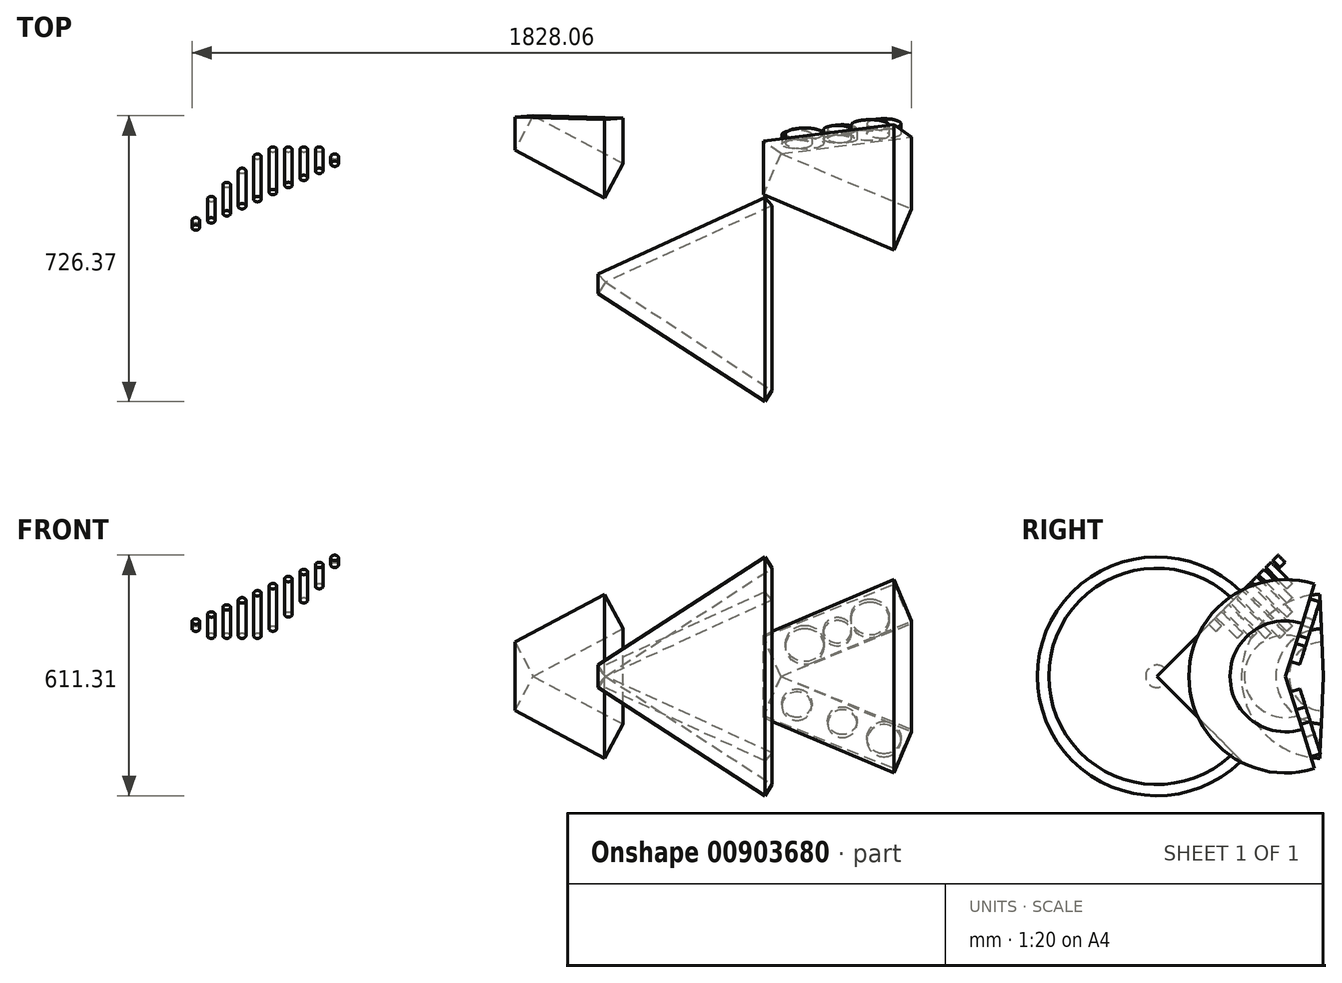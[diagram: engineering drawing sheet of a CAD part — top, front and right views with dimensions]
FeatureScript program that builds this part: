
annotation { "Feature Type Name" : "Feature", "Feature Type Description" : "" }
export const myFeature = defineFeature(function(context is Context, id is Id, definition is map)
    precondition{}
    {
        {
            var Q0;
            Q0=qCreatedBy(makeId("Top.planeOp"),FACE);
            var sketch = newSketch(context, id + "F0", { "sketchPlane" : qUnion([Q0])});
            skLineSegment(sketch, "E0.bottom", {"start": v(100.8, 8.25) * mm, "end": v(328.8, -112.98) * mm});
            skLineSegment(sketch, "E0.top", {"start": v(147.2, 95.54) * mm, "end": v(375.21, -25.7) * mm});
            skLineSegment(sketch, "E0.left", {"start": v(100.8, 8.25) * mm, "end": v(147.2, 95.54) * mm});
            skLineSegment(sketch, "E0.right", {"start": v(328.8, -112.98) * mm, "end": v(375.21, -25.7) * mm});
            skLineSegment(sketch, "E1", {"start": v(147.2, 95.54) * mm, "end": v(426, 95.54) * mm, "construction": true});
            skLineSegment(sketch, "E2", {"start": v(426, 95.54) * mm, "end": v(286.6, 95.54) * mm, "construction": true});
            skLineSegment(sketch, "E3.bottom", {"start": v(776.15, -0.71) * mm, "end": v(1108.48, -141.78) * mm});
            skLineSegment(sketch, "E3.top", {"start": v(731.8, -105.22) * mm, "end": v(1064.12, -246.28) * mm});
            skLineSegment(sketch, "E3.left", {"start": v(776.15, -0.71) * mm, "end": v(731.8, -105.22) * mm});
            skLineSegment(sketch, "E3.right", {"start": v(1108.48, -141.78) * mm, "end": v(1064.12, -246.28) * mm});
            skLineSegment(sketch, "E4.bottom", {"start": v(754.2, -602.2) * mm, "end": v(331.11, -327.43) * mm});
            skLineSegment(sketch, "E4.top", {"start": v(735.61, -630.83) * mm, "end": v(312.51, -356.07) * mm});
            skLineSegment(sketch, "E4.left", {"start": v(754.2, -602.2) * mm, "end": v(735.61, -630.83) * mm});
            skLineSegment(sketch, "E4.right", {"start": v(331.11, -327.43) * mm, "end": v(312.51, -356.07) * mm});
            skLineSegment(sketch, "E5", {"start": v(776.15, -0.71) * mm, "end": v(1137.18, -0.71) * mm, "construction": true});
            skLineSegment(sketch, "E6", {"start": v(331.11, -327.43) * mm, "end": v(835.6, -327.43) * mm, "construction": true});
            skSolve(sketch);
        }
        {
            var Q0;
            Q0=makeQuery(id+"F0.imprint","IMPRINT",FACE,{"disambiguationData":[TD([[makeQuery(id+"F0.imprint","IMPRINT",EDGE,{"derivedFrom":sQuery(id+"F0.wireOp",EDGE,"E0.bottom")}),1.0]])]});
            var Q1;
            Q1=sQuery(id+"F0.wireOp",EDGE,"E1");
            revolve(context, id + "F1", {"surfaceOperationType" : NewSurfaceOperationType.NEW, "entities" : qUnion([Q0]), "axis" : qUnion([Q1]), "revolveType" : RevolveType.SYMMETRIC, "angle" : 175 * degree});
        }
        {
            var Q0;
            Q0=makeQuery(id+"F0.imprint","IMPRINT",FACE,{"disambiguationData":[TD([[makeQuery(id+"F0.imprint","IMPRINT",EDGE,{"derivedFrom":sQuery(id+"F0.wireOp",EDGE,"E3.bottom")}),-1.0]])]});
            var Q1;
            Q1=sQuery(id+"F0.wireOp",EDGE,"E5");
            revolve(context, id + "F2", {"surfaceOperationType" : NewSurfaceOperationType.NEW, "entities" : qUnion([Q0]), "axis" : qUnion([Q1]), "revolveType" : RevolveType.SYMMETRIC, "angle" : 215 * degree});
        }
        {
            var Q0;
            Q0=makeQuery(id+"F0.imprint","IMPRINT",FACE,{"disambiguationData":[TD([[makeQuery(id+"F0.imprint","IMPRINT",EDGE,{"derivedFrom":sQuery(id+"F0.wireOp",EDGE,"E4.bottom")}),1.0]])]});
            var Q1;
            Q1=sQuery(id+"F0.wireOp",EDGE,"E6");
            revolve(context, id + "F3", {"surfaceOperationType" : NewSurfaceOperationType.NEW, "entities" : qUnion([Q0]), "axis" : qUnion([Q1]), "revolveType" : RevolveType.SYMMETRIC, "angle" : 270 * degree});
        }
        {
            var Q0;
            Q0=makeQuery(id+"F2.opRevolve","CAP_FACE",FACE,{"disambiguationData":[OSD([sQuery(id+"F0.wireOp",EDGE,"E3.bottom"),sQuery(id+"F0.wireOp",EDGE,"E3.top"),sQuery(id+"F0.wireOp",EDGE,"E3.left"),sQuery(id+"F0.wireOp",EDGE,"E3.right")])],"isStart":false});
            var sketch = newSketch(context, id + "F4", { "sketchPlane" : qUnion([Q0])});
            skCircle(sketch, "E7", {"center": v(-932.54, -125.78) * mm, "radius": 37.16 * mm});
            skCircle(sketch, "E8", {"center": v(-1038.46, -171.03) * mm, "radius": 43.1 * mm});
            skCircle(sketch, "E9", {"center": v(-817.03, -79.17) * mm, "radius": 37.88 * mm});
            skSolve(sketch);
        }
        {
            var Q0;
            Q0=makeQuery(id+"F4.imprint","IMPRINT",FACE,{"disambiguationData":[TD([[makeQuery(id+"F4.imprint","IMPRINT",EDGE,{"derivedFrom":sQuery(id+"F4.wireOp",EDGE,"E9")}),1.0]])]});
            var Q1;
            Q1=makeQuery(id+"F4.imprint","IMPRINT",FACE,{"disambiguationData":[TD([[makeQuery(id+"F4.imprint","IMPRINT",EDGE,{"derivedFrom":sQuery(id+"F4.wireOp",EDGE,"E7")}),1.0]])]});
            var Q2;
            Q2=makeQuery(id+"F4.imprint","IMPRINT",FACE,{"disambiguationData":[TD([[makeQuery(id+"F4.imprint","IMPRINT",EDGE,{"derivedFrom":sQuery(id+"F4.wireOp",EDGE,"E8")}),1.0]])]});
            extrude(context, id + "F5", {"entities" : qUnion([Q0, Q1, Q2]), "operationType" : NewBodyOperationType.ADD, "depth" : 25.4 * mm, "offsetDistance" : 25.4 * mm});
        }
        {
            var Q0;
            Q0=makeQuery(id+"F2.opRevolve","CAP_FACE",FACE,{"disambiguationData":[OSD([sQuery(id+"F0.wireOp",EDGE,"E3.bottom"),sQuery(id+"F0.wireOp",EDGE,"E3.top"),sQuery(id+"F0.wireOp",EDGE,"E3.left"),sQuery(id+"F0.wireOp",EDGE,"E3.right")])],"isStart":true});
            var sketch = newSketch(context, id + "F6", { "sketchPlane" : qUnion([Q0])});
            skLineSegment(sketch, "E10", {"start": v(-1086.3, 193.1) * mm, "end": v(-753.97, 52.04) * mm, "construction": true});
            skLineSegment(sketch, "E11", {"start": v(-897.95, 174.82) * mm, "end": v(-942.31, 70.32) * mm, "construction": true});
            skLineSegment(sketch, "E12", {"start": v(-814.87, 139.56) * mm, "end": v(-859.23, 35.05) * mm, "construction": true});
            skLineSegment(sketch, "E13", {"start": v(-981.04, 210.09) * mm, "end": v(-1025.4, 105.58) * mm});
            skLineSegment(sketch, "E14.0", {"start": v(-731.8, 104.29) * mm, "end": v(-814.87, 139.56) * mm});
            skLineSegment(sketch, "E15.0", {"start": v(-776.15, -0.21) * mm, "end": v(-1108.48, 140.85) * mm});
            skLineSegment(sketch, "E16.0", {"start": v(-776.15, -0.21) * mm, "end": v(-731.8, 104.29) * mm});
            skLineSegment(sketch, "E17.0", {"start": v(-1108.48, 140.85) * mm, "end": v(-1064.12, 245.35) * mm});
            skLineSegment(sketch, "E18", {"start": v(-897.95, 174.82) * mm, "end": v(-1064.12, 245.35) * mm});
            skLineSegment(sketch, "E19", {"start": v(-814.87, 139.56) * mm, "end": v(-897.95, 174.82) * mm});
            skCircle(sketch, "E20", {"center": v(-1003.22, 157.84) * mm, "radius": 48.44 * mm});
            skCircle(sketch, "E21", {"center": v(-920.13, 122.57) * mm, "radius": 35 * mm});
            skCircle(sketch, "E22", {"center": v(-837.05, 87.3) * mm, "radius": 48.44 * mm});
            skSolve(sketch);
        }
        {
            var Q0;
            Q0=makeQuery(id+"F6.imprint","IMPRINT",FACE,{"disambiguationData":[TD([[makeQuery(id+"F6.imprint","IMPRINT",EDGE,{"derivedFrom":sQuery(id+"F6.wireOp",EDGE,"E22")}),1.0]])]});
            var Q1;
            Q1=makeQuery(id+"F6.imprint","IMPRINT",FACE,{"disambiguationData":[TD([[makeQuery(id+"F6.imprint","IMPRINT",EDGE,{"derivedFrom":sQuery(id+"F6.wireOp",EDGE,"E21")}),1.0]])]});
            var Q2;
            {var subQ0=sQuery(id+"F6.wireOp",EDGE,"E20");var subQ1=sQuery(id+"F6.wireOp",EDGE,"E13");var subQ2=makeQuery(id+"F6.imprint","INTERSECT",VERTEX,{"disambiguationData":[OD(0.0)],"derivedFrom":[subQ1,subQ0]});Q2=makeQuery(id+"F6.imprint","IMPRINT",FACE,{"disambiguationData":[TD([[makeQuery(id+"F6.imprint","IMPRINT",EDGE,{"disambiguationData":[TD([[subQ2,-1.0]])],"derivedFrom":subQ1}),1.0]])]});}
            var Q3;
            {var subQ0=sQuery(id+"F6.wireOp",EDGE,"E20");var subQ1=sQuery(id+"F6.wireOp",EDGE,"E13");var subQ2=makeQuery(id+"F6.imprint","INTERSECT",VERTEX,{"disambiguationData":[OD(0.0)],"derivedFrom":[subQ1,subQ0]});Q3=makeQuery(id+"F6.imprint","IMPRINT",FACE,{"disambiguationData":[TD([[makeQuery(id+"F6.imprint","IMPRINT",EDGE,{"disambiguationData":[TD([[subQ2,-1.0]])],"derivedFrom":subQ1}),-1.0]])]});}
            extrude(context, id + "F7", {"entities" : qUnion([Q0, Q1, Q2, Q3]), "operationType" : NewBodyOperationType.ADD, "depth" : 25.4 * mm, "offsetDistance" : 25.4 * mm});
        }
        {
            var Q0;
            Q0=makeQuery(id+"F3.opRevolve","CAP_FACE",FACE,{"disambiguationData":[OSD([sQuery(id+"F0.wireOp",EDGE,"E4.bottom"),sQuery(id+"F0.wireOp",EDGE,"E4.top"),sQuery(id+"F0.wireOp",EDGE,"E4.left"),sQuery(id+"F0.wireOp",EDGE,"E4.right")])],"isStart":true});
            var sketch = newSketch(context, id + "F8", { "sketchPlane" : qUnion([Q0])});
            skLineSegment(sketch, "E23.0", {"start": v(735.61, -71.87) * mm, "end": v(312.51, 202.9) * mm});
            skLineSegment(sketch, "E24.0", {"start": v(754.2, -43.23) * mm, "end": v(331.11, 231.53) * mm});
            skLineSegment(sketch, "E25.0", {"start": v(331.11, 231.53) * mm, "end": v(312.51, 202.9) * mm});
            skLineSegment(sketch, "E26.0", {"start": v(754.2, -43.23) * mm, "end": v(735.61, -71.87) * mm});
            skCircle(sketch, "E27", {"center": v(709.88, -34.8) * mm, "radius": 9.7 * mm});
            skCircle(sketch, "E28.1.0.0", {"center": v(670.7, -9.36) * mm, "radius": 9.7 * mm});
            skCircle(sketch, "E28.2.0.0", {"center": v(631.51, 16.1) * mm, "radius": 9.7 * mm});
            skCircle(sketch, "E28.3.0.0", {"center": v(592.33, 41.54) * mm, "radius": 9.7 * mm});
            skCircle(sketch, "E28.4.0.0", {"center": v(553.14, 66.98) * mm, "radius": 9.7 * mm});
            skCircle(sketch, "E28.5.0.0", {"center": v(513.96, 92.43) * mm, "radius": 9.7 * mm});
            skCircle(sketch, "E28.6.0.0", {"center": v(474.77, 117.88) * mm, "radius": 9.7 * mm});
            skCircle(sketch, "E28.7.0.0", {"center": v(435.6, 143.32) * mm, "radius": 9.7 * mm});
            skCircle(sketch, "E28.8.0.0", {"center": v(396.4, 168.77) * mm, "radius": 9.7 * mm});
            skCircle(sketch, "E28.9.0.0", {"center": v(357.22, 194.22) * mm, "radius": 9.7 * mm});
            skLineSegment(sketch, "E28.direction1", {"start": v(709.88, -34.8) * mm, "end": v(670.7, -9.36) * mm, "construction": true});
            skLineSegment(sketch, "E29", {"start": v(321.81, 217.21) * mm, "end": v(744.91, -57.55) * mm, "construction": true});
            skSolve(sketch);
        }
        {
            var Q0;
            Q0=makeQuery(id+"F8.imprint","IMPRINT",FACE,{"disambiguationData":[TD([[makeQuery(id+"F8.imprint","IMPRINT",EDGE,{"derivedFrom":sQuery(id+"F8.wireOp",EDGE,"E27")}),1.0]])]});
            var Q1;
            Q1=makeQuery(id+"F8.imprint","IMPRINT",FACE,{"disambiguationData":[TD([[makeQuery(id+"F8.imprint","IMPRINT",EDGE,{"derivedFrom":sQuery(id+"F8.wireOp",EDGE,"E28.1.0.0")}),1.0]])]});
            var Q2;
            Q2=makeQuery(id+"F8.imprint","IMPRINT",FACE,{"disambiguationData":[TD([[makeQuery(id+"F8.imprint","IMPRINT",EDGE,{"derivedFrom":sQuery(id+"F8.wireOp",EDGE,"E28.2.0.0")}),1.0]])]});
            var Q3;
            Q3=makeQuery(id+"F8.imprint","IMPRINT",FACE,{"disambiguationData":[TD([[makeQuery(id+"F8.imprint","IMPRINT",EDGE,{"derivedFrom":sQuery(id+"F8.wireOp",EDGE,"E28.3.0.0")}),1.0]])]});
            var Q4;
            Q4=makeQuery(id+"F8.imprint","IMPRINT",FACE,{"disambiguationData":[TD([[makeQuery(id+"F8.imprint","IMPRINT",EDGE,{"derivedFrom":sQuery(id+"F8.wireOp",EDGE,"E28.4.0.0")}),1.0]])]});
            var Q5;
            Q5=makeQuery(id+"F8.imprint","IMPRINT",FACE,{"disambiguationData":[TD([[makeQuery(id+"F8.imprint","IMPRINT",EDGE,{"derivedFrom":sQuery(id+"F8.wireOp",EDGE,"E28.5.0.0")}),1.0]])]});
            var Q6;
            Q6=makeQuery(id+"F8.imprint","IMPRINT",FACE,{"disambiguationData":[TD([[makeQuery(id+"F8.imprint","IMPRINT",EDGE,{"derivedFrom":sQuery(id+"F8.wireOp",EDGE,"E28.6.0.0")}),1.0]])]});
            var Q7;
            Q7=makeQuery(id+"F8.imprint","IMPRINT",FACE,{"disambiguationData":[TD([[makeQuery(id+"F8.imprint","IMPRINT",EDGE,{"derivedFrom":sQuery(id+"F8.wireOp",EDGE,"E28.7.0.0")}),1.0]])]});
            var Q8;
            Q8=makeQuery(id+"F8.imprint","IMPRINT",FACE,{"disambiguationData":[TD([[makeQuery(id+"F8.imprint","IMPRINT",EDGE,{"derivedFrom":sQuery(id+"F8.wireOp",EDGE,"E28.8.0.0")}),1.0]])]});
            var Q9;
            Q9=makeQuery(id+"F8.imprint","IMPRINT",FACE,{"disambiguationData":[TD([[makeQuery(id+"F8.imprint","IMPRINT",EDGE,{"derivedFrom":sQuery(id+"F8.wireOp",EDGE,"E28.9.0.0")}),1.0]])]});
            extrude(context, id + "F9", {"entities" : qUnion([Q0, Q1, Q2, Q3, Q4, Q5, Q6, Q7, Q8, Q9]), "operationType" : NewBodyOperationType.ADD, "depth" : 25.4 * mm, "offsetDistance" : 25.4 * mm});
        }
        {
            var Q0;
            Q0=makeQuery(id+"F9.opExtrude","CAP_FACE",FACE,{"disambiguationData":[OSD([sQuery(id+"F8.wireOp",EDGE,"E28.1.0.0")])],"isStart":false});
            var Q1;
            Q1=makeQuery(id+"F9.opExtrude","CAP_FACE",FACE,{"disambiguationData":[OSD([sQuery(id+"F8.wireOp",EDGE,"E28.8.0.0")])],"isStart":false});
            extrude(context, id + "F10", {"entities" : qUnion([Q0, Q1]), "operationType" : NewBodyOperationType.ADD, "depth" : 50.8 * mm, "offsetDistance" : 25.4 * mm});
        }
        {
            var Q0;
            Q0=makeQuery(id+"F9.opExtrude","CAP_FACE",FACE,{"disambiguationData":[OSD([sQuery(id+"F8.wireOp",EDGE,"E28.7.0.0")])],"isStart":false});
            var Q1;
            Q1=makeQuery(id+"F9.opExtrude","CAP_FACE",FACE,{"disambiguationData":[OSD([sQuery(id+"F8.wireOp",EDGE,"E28.2.0.0")])],"isStart":false});
            extrude(context, id + "F11", {"entities" : qUnion([Q0, Q1]), "operationType" : NewBodyOperationType.ADD, "depth" : 76.2 * mm, "offsetDistance" : 25.4 * mm});
        }
        {
            var Q0;
            Q0=makeQuery(id+"F9.opExtrude","CAP_FACE",FACE,{"disambiguationData":[OSD([sQuery(id+"F8.wireOp",EDGE,"E28.3.0.0")])],"isStart":false});
            var Q1;
            Q1=makeQuery(id+"F9.opExtrude","CAP_FACE",FACE,{"disambiguationData":[OSD([sQuery(id+"F8.wireOp",EDGE,"E28.6.0.0")])],"isStart":false});
            extrude(context, id + "F12", {"entities" : qUnion([Q0, Q1]), "operationType" : NewBodyOperationType.ADD, "depth" : 101.6 * mm, "offsetDistance" : 25.4 * mm});
        }
        {
            var Q0;
            Q0=makeQuery(id+"F9.opExtrude","CAP_FACE",FACE,{"disambiguationData":[OSD([sQuery(id+"F8.wireOp",EDGE,"E28.5.0.0")])],"isStart":false});
            var Q1;
            Q1=makeQuery(id+"F9.opExtrude","CAP_FACE",FACE,{"disambiguationData":[OSD([sQuery(id+"F8.wireOp",EDGE,"E28.4.0.0")])],"isStart":false});
            extrude(context, id + "F13", {"entities" : qUnion([Q0, Q1]), "operationType" : NewBodyOperationType.ADD, "depth" : 127 * mm, "offsetDistance" : 25.4 * mm});
        }
    });
